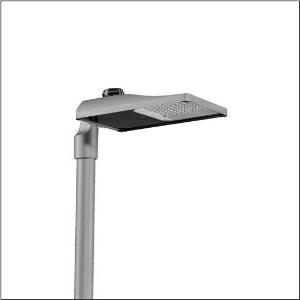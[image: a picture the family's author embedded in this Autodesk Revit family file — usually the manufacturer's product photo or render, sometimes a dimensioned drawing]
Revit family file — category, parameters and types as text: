
# Revit family: streetlight_sl_31_midi___st0_5a_5xh7b75n08na_00dd
name_source: partatom
category: Lighting Fixtures
units: mm (PartAtom-declared; Revit-internal decimal feet)

## family parameters
Cut with Voids When Loaded = No
Host = Face
Light Source = No
Part Type = Normal
Room Calculation Point = No
Round Connector Dimension = Use Diameter
Shared = No

## types (1)
- --- (1 x LED, 18640 lm, 149.4 W, 2200K)
    Apparent Load = 149 VA
    CIE Flux Codes = 43 76 97 100 100
    Color Rendering = 70
    Color Temperature = 2200K
    Default Elevation = 1800 mm
    Description = Streetlight SL 31 midi NEMA (7pin), Desk-Remote mast luminaire for post-top, side-entry; light control with lens of PMMA; light distribution: ST0.5a, direct asymmetric distribution, for standard-compliant lighting for roads and squares; LED: luminous flux: 18.640lm, light colour: 722, colour temperature: 2200K; luminous efficacy: 124,8lm/W; control: pre-setting: linear dimming characteristic, flexible luminous flux parameterisation, time-dependent luminous flux control, constant luminous flux control, intelligent temperature release in ECG and LED module, overheat protection; luminaire housing, of diecast aluminium, Siteco® metallic grey (DB 702S), corrosivity category C5 high according to DIN EN ISO 12944; cover of toughened safety glass, transparent, opened without tools; mast flange of diecast aluminium, Siteco® metallic grey (DB 702S), spigot size: 76/60mm, mast flange included unmounted; with cable H07RN-F 3x 1.5mm², cable length: 12,5m, connection cable pre-assembled; mains connection: 220..240V, AC, 50/60Hz; power consumption (at start of service life): 149,4W / (at end of service life): 163,4W / (with reduced operation 50%): 66,1W; protection rating (complete): IP66; insulation class (complete): insulation class I (protective earthing); impact resistance: IK10; certification: CE, ENEC, ENEC+, VDE, UKCA; permissible operating ambient temperature for outdoor applications: -40..+50°C; packaging unit: 1 piece

Light Distribution: ST0.5a
    Height = 79 mm
    Lamp = 1 x LED
    Lamp Light Flux = 18640 lm
    Lamp Power = 149.4 W
    Lamp count = 1
    Length = 577 mm
    Luminous efficacy = 125 lm/W
    Manufacturer = Siteco
    ModVariant = No
    Model = 5XH7B75N08NA
    Number of Poles = 1
    OnlyDefault = Yes
    Power Factor = 1
    Product Name = Streetlight SL 31 midi | ST0.5a
    Product group = mast luminaire | pylon top
    ProductGroupID = 6100
    Protection Class = Protection class I
    Protection Degree = IP 66
    RLX_Detail_Level = 1
    RLX_Emergency_Light_Flux = 0 lm
    RLX_Emergency_Type = 0
    RLX_Emergency_Type_DB = No
    RlxData = <blob elided: 54385 chars, md5=37fc295b>
    Socket = socket
    Standby Power = 0 W
    System Light Flux = 18641 lm
    System Power = 149 W
    Type Comments = factory setting: luminous flux: 100 % | dim-lin: 254 | 796 mA
    Type Image = l_1300282.jpg
    URL = http://relux.com
    VarID = @adj_057446
    Voltage = 0 V
    Weight = 0.00 kg
    Width = 362 mm

## geometry (parser evidence)
native form markers: Blend x4, Sweep x11
no freeform markers — native parametric forms only
